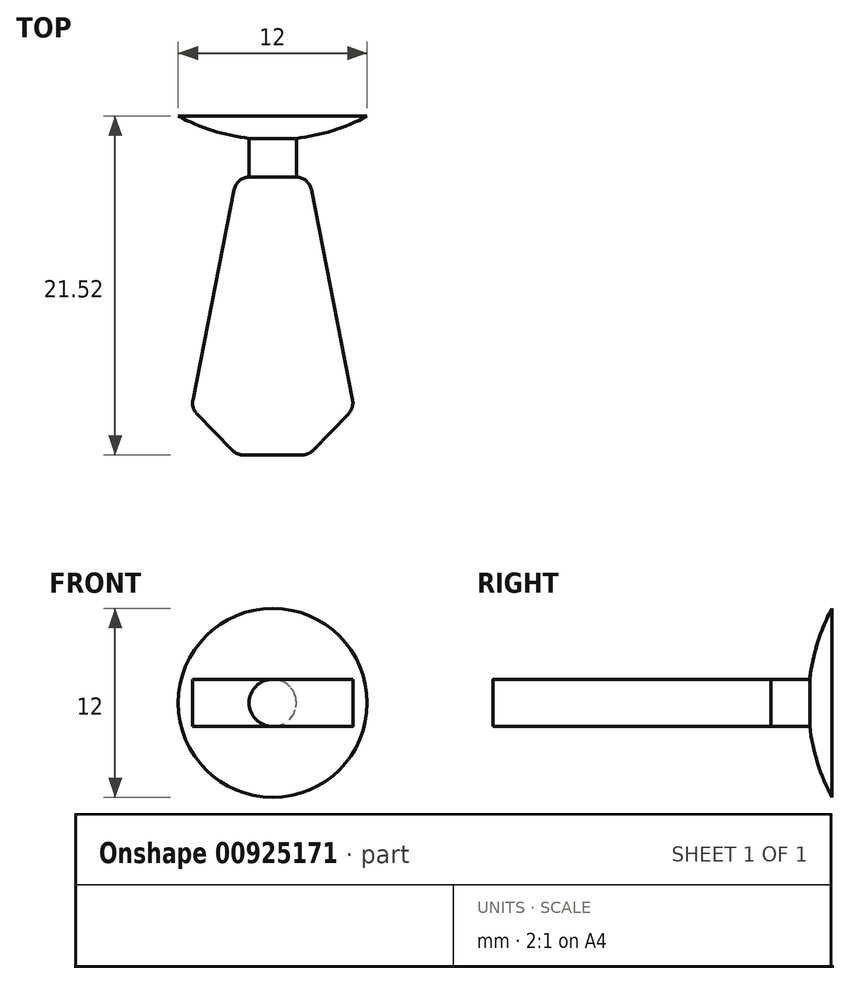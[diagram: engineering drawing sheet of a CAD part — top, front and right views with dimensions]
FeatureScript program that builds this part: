
annotation { "Feature Type Name" : "Feature", "Feature Type Description" : "" }
export const myFeature = defineFeature(function(context is Context, id is Id, definition is map)
    precondition{}
    {
        {
            var Q0;
            Q0=qCreatedBy(makeId("Right.planeOp"),FACE);
            var sketch = newSketch(context, id + "F0", { "sketchPlane" : qUnion([Q0])});
            skLineSegment(sketch, "E0", {"start": v(0, 6) * mm, "end": v(0, 0) * mm});
            skArc(sketch, "E1", {"start": v(0, 6) * mm, "mid": v(-1.12, 3.1) * mm, "end": v(-1.5, 0) * mm});
            skLineSegment(sketch, "E2", {"start": v(-17.4, 0) * mm, "end": v(19.26, 0) * mm, "construction": true});
            skLineSegment(sketch, "E3", {"start": v(-1.5, 0) * mm, "end": v(0, 0) * mm});
            skPoint(sketch, "E4.orphan", {"position": v(0, -6) * mm});
            skSolve(sketch);
        }
        {
            var Q0;
            Q0 = qSketchRegion(id + "F0", true);
            var Q1;
            Q1=sQuery(id+"F0.wireOp",EDGE,"E2");
            revolve(context, id + "F1", {"surfaceOperationType" : NewSurfaceOperationType.NEW, "entities" : qUnion([Q0]), "axis" : qUnion([Q1]), "revolveType" : RevolveType.FULL});
        }
        {
            var Q0;
            Q0=qCreatedBy(makeId("Front.planeOp"),FACE);
            var sketch = newSketch(context, id + "F2", { "sketchPlane" : qUnion([Q0])});
            skCircle(sketch, "E5", {"center": v(0, 0) * mm, "radius": 1.5 * mm});
            skSolve(sketch);
        }
        {
            var Q0;
            Q0 = qSketchRegion(id + "F2", true);
            extrude(context, id + "F3", {"entities" : qUnion([Q0]), "operationType" : NewBodyOperationType.ADD, "depth" : 4 * mm, "offsetDistance" : 25 * mm});
        }
        {
            var Q0;
            Q0=qCreatedBy(makeId("Top.planeOp"),FACE);
            var sketch = newSketch(context, id + "F4", { "sketchPlane" : qUnion([Q0])});
            skLineSegment(sketch, "E6", {"start": v(0, -3.87) * mm, "end": v(-1.47, -3.87) * mm});
            skLineSegment(sketch, "E7", {"start": v(-2.45, -4.67) * mm, "end": v(-5.07, -18.03) * mm});
            skLineSegment(sketch, "E8", {"start": v(-4.8, -18.91) * mm, "end": v(-2.59, -21.21) * mm});
            skLineSegment(sketch, "E9", {"start": v(-1.87, -21.52) * mm, "end": v(0, -21.52) * mm});
            skLineSegment(sketch, "E10", {"start": v(0, -27.33) * mm, "end": v(0, 13.26) * mm, "construction": true});
            skPoint(sketch, "E11.visualSharp", {"position": v(-5.17, -18.54) * mm});
            skArc(sketch, "E11.filletArc", {"start": v(-5.07, -18.03) * mm, "mid": v(-5.05, -18.5) * mm, "end": v(-4.8, -18.91) * mm});
            skPoint(sketch, "E12.visualSharp", {"position": v(-2.3, -21.52) * mm});
            skArc(sketch, "E12.filletArc", {"start": v(-2.59, -21.21) * mm, "mid": v(-2.26, -21.44) * mm, "end": v(-1.87, -21.52) * mm});
            skPoint(sketch, "E13.visualSharp", {"position": v(-2.3, -3.87) * mm});
            skArc(sketch, "E13.filletArc", {"start": v(-1.47, -3.87) * mm, "mid": v(-2.1, -4.1) * mm, "end": v(-2.45, -4.67) * mm});
            skArc(sketch, "E14.MirrorCS", {"start": v(5.07, -18.03) * mm, "mid": v(5.05, -18.5) * mm, "end": v(4.8, -18.91) * mm});
            skArc(sketch, "E15.MirrorCS", {"start": v(2.59, -21.21) * mm, "mid": v(2.26, -21.44) * mm, "end": v(1.87, -21.52) * mm});
            skArc(sketch, "E16.MirrorCS", {"start": v(1.47, -3.87) * mm, "mid": v(2.1, -4.1) * mm, "end": v(2.45, -4.67) * mm});
            skPoint(sketch, "E17.MirrorP", {"position": v(2.3, -3.87) * mm});
            skPoint(sketch, "E18.MirrorP", {"position": v(2.3, -21.52) * mm});
            skLineSegment(sketch, "E19.MirrorCS", {"start": v(0, -3.87) * mm, "end": v(1.47, -3.87) * mm});
            skLineSegment(sketch, "E20.MirrorCS", {"start": v(1.87, -21.52) * mm, "end": v(0, -21.52) * mm});
            skLineSegment(sketch, "E21.MirrorCS", {"start": v(4.8, -18.91) * mm, "end": v(2.59, -21.21) * mm});
            skLineSegment(sketch, "E22.MirrorCS", {"start": v(2.45, -4.67) * mm, "end": v(5.07, -18.03) * mm});
            skPoint(sketch, "E23.MirrorP", {"position": v(5.17, -18.54) * mm});
            skSolve(sketch);
        }
        {
            var Q0;
            Q0 = qSketchRegion(id + "F4", true);
            extrude(context, id + "F5", {"entities" : qUnion([Q0]), "operationType" : NewBodyOperationType.ADD, "depth" : 3 * mm, "offsetDistance" : 25 * mm, "symmetric" : true});
        }
    });
